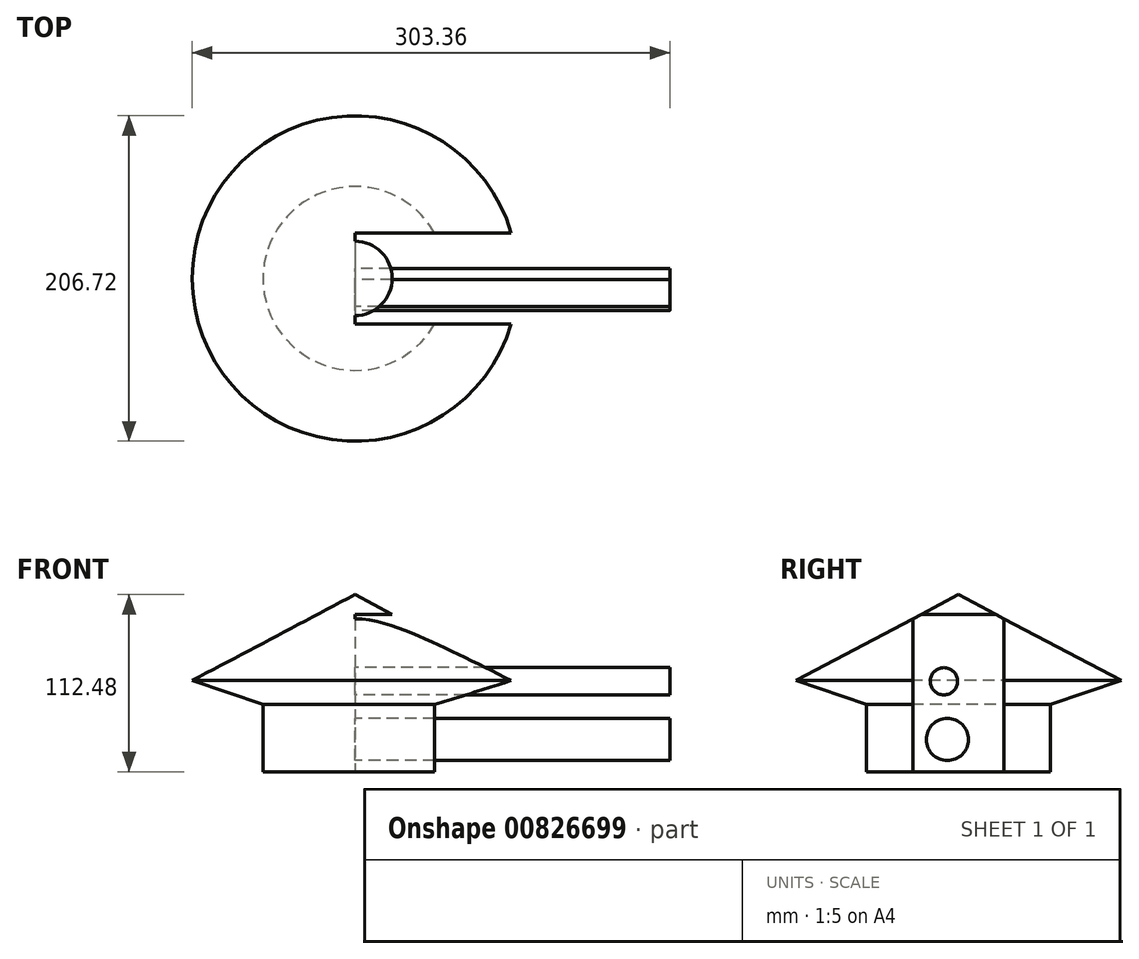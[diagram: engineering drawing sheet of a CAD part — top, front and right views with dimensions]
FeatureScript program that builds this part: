
annotation { "Feature Type Name" : "Feature", "Feature Type Description" : "" }
export const myFeature = defineFeature(function(context is Context, id is Id, definition is map)
    precondition{}
    {
        {
            var Q0;
            Q0=qCreatedBy(makeId("Front.planeOp"),FACE);
            var sketch = newSketch(context, id + "F0", { "sketchPlane" : qUnion([Q0])});
            skLineSegment(sketch, "E0", {"start": v(0, 0) * mm, "end": v(58.37, 0) * mm});
            skLineSegment(sketch, "E1", {"start": v(58.37, 0) * mm, "end": v(58.37, 42.91) * mm});
            skLineSegment(sketch, "E2", {"start": v(58.37, 42.91) * mm, "end": v(103.36, 57.92) * mm});
            skLineSegment(sketch, "E3", {"start": v(103.36, 57.92) * mm, "end": v(0, 112.48) * mm});
            skLineSegment(sketch, "E4", {"start": v(0, 112.48) * mm, "end": v(0, 0) * mm});
            skSolve(sketch);
        }
        {
            var Q0;
            Q0=makeQuery(id+"F0.imprint","IMPRINT",FACE,{"disambiguationData":[TD([[makeQuery(id+"F0.imprint","IMPRINT",EDGE,{"derivedFrom":sQuery(id+"F0.wireOp",EDGE,"E0")}),1.0]])]});
            var Q1;
            Q1=sQuery(id+"F0.wireOp",EDGE,"E4");
            revolve(context, id + "F1", {"surfaceOperationType" : NewSurfaceOperationType.NEW, "entities" : qUnion([Q0]), "axis" : qUnion([Q1]), "revolveType" : RevolveType.FULL});
        }
        {
            var Q0;
            Q0=makeQuery(id+"F1.opRevolve","SWEPT_FACE",FACE,{"disambiguationData":[OSD([sQuery(id+"F0.wireOp",EDGE,"E0")])]});
            var sketch = newSketch(context, id + "F2", { "sketchPlane" : qUnion([Q0])});
            skLineSegment(sketch, "E5.bottom", {"start": v(0, -28.95) * mm, "end": v(267.14, -28.95) * mm});
            skLineSegment(sketch, "E5.top", {"start": v(0, 28.95) * mm, "end": v(267.14, 28.95) * mm});
            skLineSegment(sketch, "E5.left", {"start": v(0, -28.95) * mm, "end": v(0, 28.95) * mm});
            skLineSegment(sketch, "E5.right", {"start": v(267.14, -28.95) * mm, "end": v(267.14, 28.95) * mm});
            skPoint(sketch, "E5.middle", {"position": v(133.57, 0) * mm});
            skSolve(sketch);
        }
        {
            var Q0;
            {var subQ0=sQuery(id+"F2.wireOp",EDGE,"E5.left");Q0=makeQuery(id+"F2.imprint","IMPRINT",FACE,{"disambiguationData":[TD([[makeQuery(id+"F2.imprint","IMPRINT",EDGE,{"derivedFrom":subQ0}),-1.0]])]});}
            var Q1;
            {var subQ0=sQuery(id+"F2.wireOp",EDGE,"E5.right");Q1=makeQuery(id+"F2.imprint","IMPRINT",FACE,{"disambiguationData":[TD([[makeQuery(id+"F2.imprint","IMPRINT",EDGE,{"derivedFrom":subQ0}),1.0]])]});}
            extrude(context, id + "F3", {"entities" : qUnion([Q0, Q1]), "operationType" : NewBodyOperationType.REMOVE, "oppositeDirection" : true, "depth" : 100 * mm, "offsetDistance" : 25 * mm});
        }
        {
            var Q0;
            Q0=makeQuery(id+"F3.boolean.opBoolean","COPY",FACE,{"derivedFrom":makeQuery(id+"F3.opExtrude","SWEPT_FACE",FACE,{"disambiguationData":[OSD([sQuery(id+"F2.wireOp",EDGE,"E5.left")])]})});
            var sketch = newSketch(context, id + "F4", { "sketchPlane" : qUnion([Q0])});
            skCircle(sketch, "E6", {"center": v(-9.29, 57.49) * mm, "radius": 8.66 * mm});
            skCircle(sketch, "E7", {"center": v(-7.07, 20.48) * mm, "radius": 13.37 * mm});
            skSolve(sketch);
        }
        {
            var Q0;
            Q0=makeQuery(id+"F4.imprint","IMPRINT",FACE,{"disambiguationData":[TD([[makeQuery(id+"F4.imprint","IMPRINT",EDGE,{"derivedFrom":sQuery(id+"F4.wireOp",EDGE,"E6")}),1.0]])]});
            var Q1;
            Q1=makeQuery(id+"F4.imprint","IMPRINT",FACE,{"disambiguationData":[TD([[makeQuery(id+"F4.imprint","IMPRINT",EDGE,{"derivedFrom":sQuery(id+"F4.wireOp",EDGE,"E7")}),1.0]])]});
            extrude(context, id + "F5", {"entities" : qUnion([Q0, Q1]), "operationType" : NewBodyOperationType.ADD, "depth" : 200 * mm, "offsetDistance" : 25 * mm});
        }
    });
